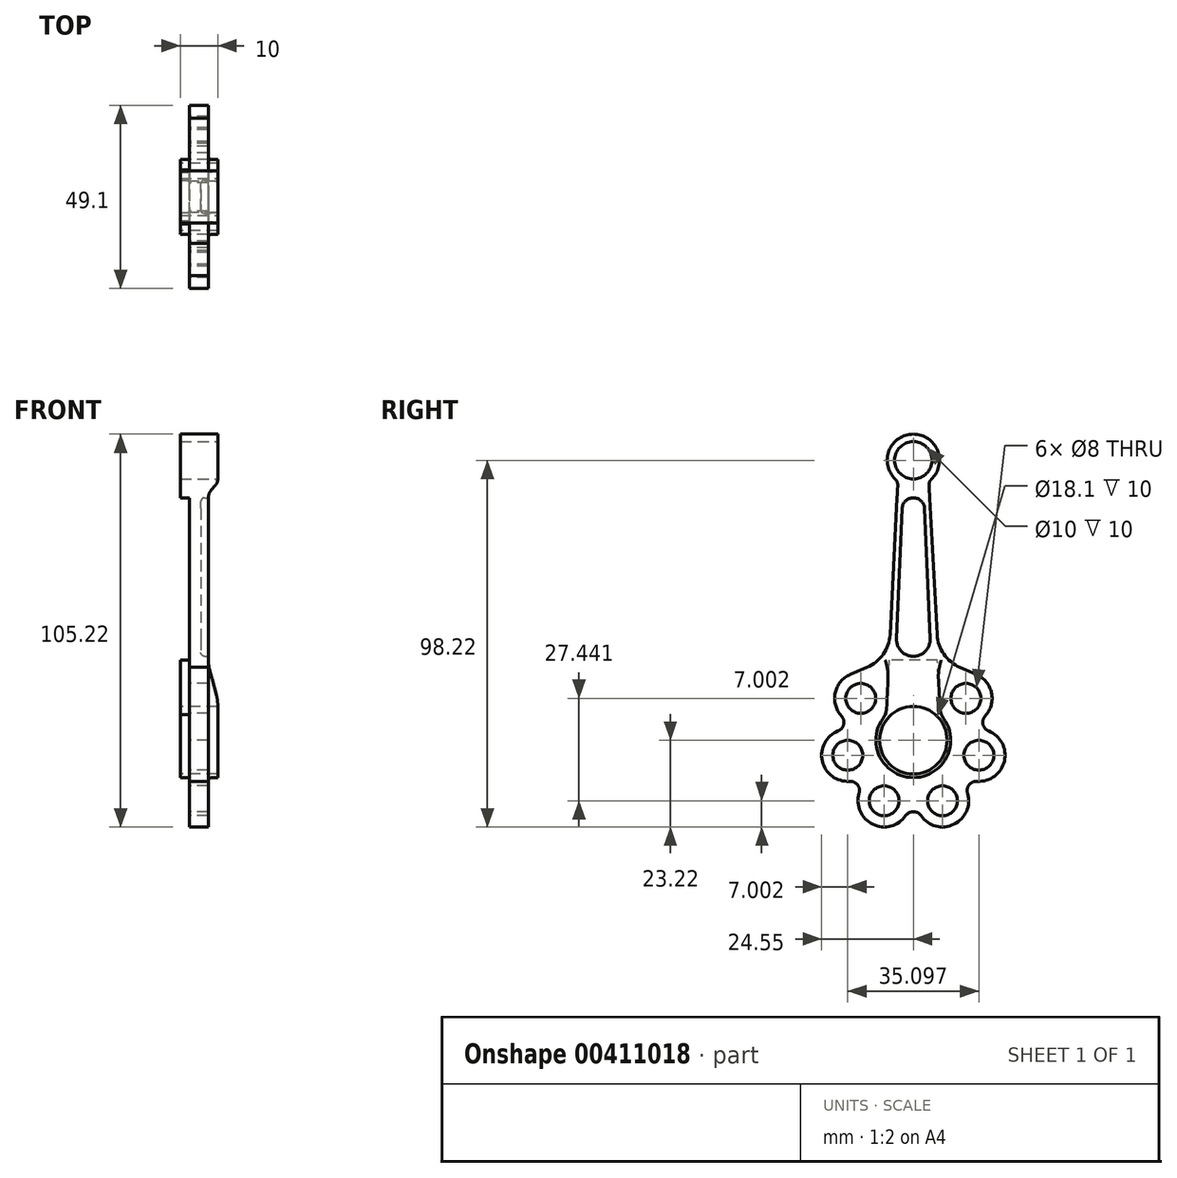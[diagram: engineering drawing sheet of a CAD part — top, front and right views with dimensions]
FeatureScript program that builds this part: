
annotation { "Feature Type Name" : "Feature", "Feature Type Description" : "" }
export const myFeature = defineFeature(function(context is Context, id is Id, definition is map)
    precondition{}
    {
        {
            var Q0;
            Q0=qCreatedBy(makeId("Right.planeOp"),FACE);
            var sketch = newSketch(context, id + "F0", { "sketchPlane" : qUnion([Q0])});
            skArc(sketch, "E0", {"start": v(-16.87, 17.64) * mm, "mid": v(-20.92, 12.68) * mm, "end": v(-19.24, 6.5) * mm});
            skArc(sketch, "E1", {"start": v(-20.15, 2.5) * mm, "mid": v(-24.37, -5.56) * mm, "end": v(-17.08, -11) * mm});
            skArc(sketch, "E2", {"start": v(-14.51, -14.2) * mm, "mid": v(-10.85, -22.53) * mm, "end": v(-2.05, -20.2) * mm});
            skArc(sketch, "E3", {"start": v(2.06, -20.2) * mm, "mid": v(10.85, -22.52) * mm, "end": v(14.52, -14.2) * mm});
            skArc(sketch, "E4", {"start": v(17.08, -11) * mm, "mid": v(24.37, -5.56) * mm, "end": v(20.15, 2.5) * mm});
            skArc(sketch, "E5", {"start": v(-20.15, 2.5) * mm, "mid": v(-18.65, 4.26) * mm, "end": v(-19.24, 6.5) * mm});
            skCircle(sketch, "E6", {"center": v(0, 0) * mm, "radius": 18 * mm, "construction": true});
            skLineSegment(sketch, "E7", {"start": v(0, 0) * mm, "end": v(0, 18) * mm, "construction": true});
            skLineSegment(sketch, "E8", {"start": v(0, 0) * mm, "end": v(-14.07, 11.22) * mm, "construction": true});
            skLineSegment(sketch, "E9", {"start": v(-17.55, -4) * mm, "end": v(0, 0) * mm, "construction": true});
            skLineSegment(sketch, "E10", {"start": v(0, 0) * mm, "end": v(-7.8, -16.22) * mm, "construction": true});
            skLineSegment(sketch, "E11", {"start": v(0, 0) * mm, "end": v(7.81, -16.22) * mm, "construction": true});
            skLineSegment(sketch, "E12", {"start": v(0, 0) * mm, "end": v(17.55, -4) * mm, "construction": true});
            skArc(sketch, "E13", {"start": v(19.24, 6.5) * mm, "mid": v(20.92, 12.68) * mm, "end": v(16.87, 17.64) * mm});
            skLineSegment(sketch, "E14", {"start": v(14.07, 11.22) * mm, "end": v(0, 0) * mm, "construction": true});
            skArc(sketch, "E15", {"start": v(-14.51, -14.2) * mm, "mid": v(-14.95, -11.93) * mm, "end": v(-17.08, -11) * mm});
            skArc(sketch, "E16", {"start": v(2.06, -20.2) * mm, "mid": v(0, -19.13) * mm, "end": v(-2.05, -20.2) * mm});
            skArc(sketch, "E17", {"start": v(17.08, -11) * mm, "mid": v(14.96, -11.93) * mm, "end": v(14.52, -14.2) * mm});
            skArc(sketch, "E18", {"start": v(19.24, 6.5) * mm, "mid": v(18.65, 4.26) * mm, "end": v(20.15, 2.5) * mm});
            skArc(sketch, "E19", {"start": v(4.81, 69.92) * mm, "mid": v(0, 82) * mm, "end": v(-4.81, 69.92) * mm});
            skLineSegment(sketch, "E20", {"start": v(-16.87, 17.64) * mm, "end": v(-12.43, 19.57) * mm});
            skLineSegment(sketch, "E21", {"start": v(12.43, 19.57) * mm, "end": v(16.87, 17.64) * mm});
            skArc(sketch, "E22", {"start": v(-12.43, 19.57) * mm, "mid": v(-8.05, 23.03) * mm, "end": v(-6.2, 28.29) * mm});
            skArc(sketch, "E23", {"start": v(6.37, 28.29) * mm, "mid": v(8.16, 23.07) * mm, "end": v(12.43, 19.57) * mm});
            skLineSegment(sketch, "E24", {"start": v(0, 0) * mm, "end": v(-23.29, 0) * mm, "construction": true});
            skLineSegment(sketch, "E25", {"start": v(-4.19, 68.36) * mm, "end": v(-6.2, 28.29) * mm});
            skLineSegment(sketch, "E26", {"start": v(4.19, 68.35) * mm, "end": v(6.37, 28.29) * mm});
            skArc(sketch, "E27", {"start": v(-4.19, 68.36) * mm, "mid": v(-4.33, 69.2) * mm, "end": v(-4.81, 69.92) * mm});
            skArc(sketch, "E28", {"start": v(4.81, 69.92) * mm, "mid": v(4.33, 69.2) * mm, "end": v(4.19, 68.35) * mm});
            skCircle(sketch, "E29", {"center": v(-14.07, 11.22) * mm, "radius": 4 * mm});
            skCircle(sketch, "E30", {"center": v(-17.55, -4) * mm, "radius": 4 * mm});
            skCircle(sketch, "E31", {"center": v(-7.8, -16.22) * mm, "radius": 4 * mm});
            skCircle(sketch, "E32", {"center": v(7.81, -16.22) * mm, "radius": 4 * mm});
            skCircle(sketch, "E33", {"center": v(17.55, -4) * mm, "radius": 4 * mm});
            skCircle(sketch, "E34", {"center": v(14.07, 11.22) * mm, "radius": 4 * mm});
            skSolve(sketch);
        }
        {
            var Q0;
            Q0 = qSketchRegion(id + "F0", true);
            extrude(context, id + "F1", {"entities" : qUnion([Q0]), "endBound" : BoundingType.SYMMETRIC, "depth" : 5 * mm});
        }
        {
            var Q0;
            Q0=qCreatedBy(makeId("Right.planeOp"),FACE);
            var sketch = newSketch(context, id + "F2", { "sketchPlane" : qUnion([Q0])});
            skArc(sketch, "E35", {"start": v(-7.25, 6.89) * mm, "mid": v(0, -10) * mm, "end": v(7.25, 6.89) * mm});
            skLineSegment(sketch, "E36.bottom", {"start": v(-6.51, 21.5) * mm, "end": v(6.45, 21.5) * mm});
            skLineSegment(sketch, "E37", {"start": v(-7.25, 6.89) * mm, "end": v(-6.51, 21.5) * mm});
            skLineSegment(sketch, "E38", {"start": v(6.45, 21.5) * mm, "end": v(7.25, 6.89) * mm});
            skSolve(sketch);
        }
        {
            var Q0;
            Q0 = qSketchRegion(id + "F2", true);
            extrude(context, id + "F3", {"entities" : qUnion([Q0]), "operationType" : NewBodyOperationType.ADD, "endBound" : BoundingType.SYMMETRIC, "depth" : 10 * mm});
        }
        {
            var Q0;
            Q0=makeQuery(id+"F1.opExtrude","CAP_FACE",FACE,{"disambiguationData":[OSD([sQuery(id+"F0.wireOp",EDGE,"E0"),sQuery(id+"F0.wireOp",EDGE,"E1"),sQuery(id+"F0.wireOp",EDGE,"E2"),sQuery(id+"F0.wireOp",EDGE,"E3"),sQuery(id+"F0.wireOp",EDGE,"E4"),sQuery(id+"F0.wireOp",EDGE,"E5"),sQuery(id+"F0.wireOp",EDGE,"E13"),sQuery(id+"F0.wireOp",EDGE,"E15"),sQuery(id+"F0.wireOp",EDGE,"E16"),sQuery(id+"F0.wireOp",EDGE,"E17"),sQuery(id+"F0.wireOp",EDGE,"E18"),sQuery(id+"F0.wireOp",EDGE,"E19"),sQuery(id+"F0.wireOp",EDGE,"E20"),sQuery(id+"F0.wireOp",EDGE,"E21"),sQuery(id+"F0.wireOp",EDGE,"E22"),sQuery(id+"F0.wireOp",EDGE,"E23"),sQuery(id+"F0.wireOp",EDGE,"E25"),sQuery(id+"F0.wireOp",EDGE,"E26"),sQuery(id+"F0.wireOp",EDGE,"E27"),sQuery(id+"F0.wireOp",EDGE,"E28")])],"isStart":false});
            var sketch = newSketch(context, id + "F4", { "sketchPlane" : qUnion([Q0])});
            skArc(sketch, "E39", {"start": v(-4.5, 27.2) * mm, "mid": v(0, 22.5) * mm, "end": v(4.5, 27.2) * mm});
            skArc(sketch, "E40", {"start": v(3, 62.1) * mm, "mid": v(0, 64.97) * mm, "end": v(-3, 62.1) * mm});
            skLineSegment(sketch, "E41", {"start": v(-3, 62.1) * mm, "end": v(-4.5, 27.2) * mm});
            skLineSegment(sketch, "E42", {"start": v(3, 62.1) * mm, "end": v(4.5, 27.2) * mm});
            skCircle(sketch, "E43", {"center": v(0, 75) * mm, "radius": 2 * mm, "construction": true});
            skSolve(sketch);
        }
        {
            var Q0;
            Q0 = qSketchRegion(id + "F4", true);
            extrude(context, id + "F5", {"entities" : qUnion([Q0]), "operationType" : NewBodyOperationType.REMOVE, "oppositeDirection" : true, "depth" : 2 * mm});
        }
        {
            var Q0;
            Q0=makeQuery(id+"F5.boolean.opBoolean","COPY",FACE,{"derivedFrom":makeQuery(id+"F5.opExtrude","CAP_FACE",FACE,{"disambiguationData":[OSD([sQuery(id+"F4.wireOp",EDGE,"E39"),sQuery(id+"F4.wireOp",EDGE,"E40"),sQuery(id+"F4.wireOp",EDGE,"E41"),sQuery(id+"F4.wireOp",EDGE,"E42")])],"isStart":false})});
            fillet(context, id + "F6", {"entities" : qUnion([Q0]), "radius" : 1 * mm, "tangentPropagation" : true, "allowEdgeOverflow" : false});
        }
        {
            var Q0;
            Q0=qCreatedBy(makeId("Right.planeOp"),FACE);
            var sketch = newSketch(context, id + "F7", { "sketchPlane" : qUnion([Q0])});
            skCircle(sketch, "E44", {"center": v(0, 0) * mm, "radius": 9.05 * mm});
            skSolve(sketch);
        }
        {
            var Q0;
            Q0 = qSketchRegion(id + "F7", true);
            extrude(context, id + "F8", {"entities" : qUnion([Q0]), "operationType" : NewBodyOperationType.REMOVE, "endBound" : BoundingType.SYMMETRIC, "depth" : 25 * mm});
        }
        {
            var Q0;
            Q0=qCreatedBy(makeId("Front.planeOp"),FACE);
            var sketch = newSketch(context, id + "F9", { "sketchPlane" : qUnion([Q0])});
            skLineSegment(sketch, "E45", {"start": v(4.66, 12.13) * mm, "end": v(2.84, 18.91) * mm});
            skLineSegment(sketch, "E46", {"start": v(2.5, 21.5) * mm, "end": v(2.5, 24) * mm, "construction": true});
            skArc(sketch, "E47", {"start": v(21.38, -48.57) * mm, "mid": v(20.84, -45.33) * mm, "end": v(19.28, -42.44) * mm});
            skArc(sketch, "E48", {"start": v(2.5, 21.5) * mm, "mid": v(2.59, 20.2) * mm, "end": v(2.84, 18.91) * mm});
            skLineSegment(sketch, "E49", {"start": v(5, 9.54) * mm, "end": v(5, 21.5) * mm});
            skLineSegment(sketch, "E50.trimOffspring", {"start": v(5, 21.5) * mm, "end": v(2.5, 21.5) * mm});
            skArc(sketch, "E51", {"start": v(5, 9.54) * mm, "mid": v(4.91, 10.84) * mm, "end": v(4.66, 12.13) * mm});
            skSolve(sketch);
        }
        {
            var Q0;
            Q0 = qSketchRegion(id + "F9", true);
            extrude(context, id + "F10", {"entities" : qUnion([Q0]), "operationType" : NewBodyOperationType.REMOVE, "endBound" : BoundingType.SYMMETRIC, "oppositeDirection" : true, "depth" : 25 * mm, "hasSecondDirection" : true, "secondDirectionOppositeDirection" : false, "secondDirectionDepth" : 25 * mm});
        }
        {
            var Q0;
            {var subQ0=sQuery(id+"F2.wireOp",EDGE,"E35");var subQ1=sQuery(id+"F2.wireOp",EDGE,"E36.right");Q0=makeQuery(id+"F3.boolean.opBoolean","SPLIT",EDGE,{"disambiguationData":[TD([makeQuery(id+"F3.opExtrude","CAP_FACE",FACE,{"disambiguationData":[OSD([subQ0,sQuery(id+"F2.wireOp",EDGE,"E36.bottom"),sQuery(id+"F2.wireOp",EDGE,"E36.left"),subQ1])],"isStart":false})])],"derivedFrom":makeQuery(id+"F3.opExtrude","SWEPT_EDGE",EDGE,{"disambiguationData":[OSD([subQ0,subQ1])]})});}
            var Q1;
            {var subQ0=sQuery(id+"F2.wireOp",EDGE,"E36.left");var subQ1=sQuery(id+"F2.wireOp",EDGE,"E35");Q1=makeQuery(id+"F3.boolean.opBoolean","SPLIT",EDGE,{"disambiguationData":[TD([makeQuery(id+"F3.opExtrude","CAP_FACE",FACE,{"disambiguationData":[OSD([subQ1,sQuery(id+"F2.wireOp",EDGE,"E36.bottom"),subQ0,sQuery(id+"F2.wireOp",EDGE,"E36.right")])],"isStart":false})])],"derivedFrom":makeQuery(id+"F3.opExtrude","SWEPT_EDGE",EDGE,{"disambiguationData":[OSD([subQ1,subQ0])]})});}
            fillet(context, id + "F11", {"entities" : qUnion([Q0, Q1]), "radius" : 5 * mm, "tangentPropagation" : true, "allowEdgeOverflow" : false});
        }
        {
            var Q0;
            Q0=makeQuery(id+"F3.boolean.opBoolean","INTERSECT",EDGE,{"derivedFrom":[makeQuery(id+"F1.opExtrude","CAP_FACE",FACE,{"disambiguationData":[OSD([sQuery(id+"F0.wireOp",EDGE,"E0"),sQuery(id+"F0.wireOp",EDGE,"E1"),sQuery(id+"F0.wireOp",EDGE,"E2"),sQuery(id+"F0.wireOp",EDGE,"E3"),sQuery(id+"F0.wireOp",EDGE,"E4"),sQuery(id+"F0.wireOp",EDGE,"E5"),sQuery(id+"F0.wireOp",EDGE,"E13"),sQuery(id+"F0.wireOp",EDGE,"E15"),sQuery(id+"F0.wireOp",EDGE,"E16"),sQuery(id+"F0.wireOp",EDGE,"E17"),sQuery(id+"F0.wireOp",EDGE,"E18"),sQuery(id+"F0.wireOp",EDGE,"E19"),sQuery(id+"F0.wireOp",EDGE,"E20"),sQuery(id+"F0.wireOp",EDGE,"E21"),sQuery(id+"F0.wireOp",EDGE,"E22"),sQuery(id+"F0.wireOp",EDGE,"E23"),sQuery(id+"F0.wireOp",EDGE,"E25"),sQuery(id+"F0.wireOp",EDGE,"E26"),sQuery(id+"F0.wireOp",EDGE,"E27"),sQuery(id+"F0.wireOp",EDGE,"E28")])],"isStart":false}),makeQuery(id+"F3.opExtrude","SWEPT_FACE",FACE,{"disambiguationData":[OSD([sQuery(id+"F2.wireOp",EDGE,"E36.left")])]})]});
            var Q1;
            {var subQ0=makeQuery(id+"F1.opExtrude","CAP_FACE",FACE,{"disambiguationData":[OSD([sQuery(id+"F0.wireOp",EDGE,"E0"),sQuery(id+"F0.wireOp",EDGE,"E1"),sQuery(id+"F0.wireOp",EDGE,"E2"),sQuery(id+"F0.wireOp",EDGE,"E3"),sQuery(id+"F0.wireOp",EDGE,"E4"),sQuery(id+"F0.wireOp",EDGE,"E5"),sQuery(id+"F0.wireOp",EDGE,"E13"),sQuery(id+"F0.wireOp",EDGE,"E15"),sQuery(id+"F0.wireOp",EDGE,"E16"),sQuery(id+"F0.wireOp",EDGE,"E17"),sQuery(id+"F0.wireOp",EDGE,"E18"),sQuery(id+"F0.wireOp",EDGE,"E19"),sQuery(id+"F0.wireOp",EDGE,"E20"),sQuery(id+"F0.wireOp",EDGE,"E21"),sQuery(id+"F0.wireOp",EDGE,"E22"),sQuery(id+"F0.wireOp",EDGE,"E23"),sQuery(id+"F0.wireOp",EDGE,"E25"),sQuery(id+"F0.wireOp",EDGE,"E26"),sQuery(id+"F0.wireOp",EDGE,"E27"),sQuery(id+"F0.wireOp",EDGE,"E28")])],"isStart":false});var subQ1=sQuery(id+"F2.wireOp",EDGE,"E36.left");var subQ2=sQuery(id+"F2.wireOp",EDGE,"E35");Q1=makeQuery(id+"F11.opFillet","BLEND_EDGE",EDGE,{"blendedFrom":[makeQuery(id+"F3.boolean.opBoolean","SPLIT",EDGE,{"disambiguationData":[TD([makeQuery(id+"F3.opExtrude","CAP_FACE",FACE,{"disambiguationData":[OSD([subQ2,sQuery(id+"F2.wireOp",EDGE,"E36.bottom"),subQ1,sQuery(id+"F2.wireOp",EDGE,"E36.right")])],"isStart":false})])],"derivedFrom":makeQuery(id+"F3.opExtrude","SWEPT_EDGE",EDGE,{"disambiguationData":[OSD([subQ2,subQ1])]})}),subQ0],"blendedInto":[subQ0]});}
            fillet(context, id + "F12", {"entities" : qUnion([Q0, Q1]), "radius" : 1 * mm, "tangentPropagation" : true, "allowEdgeOverflow" : false});
        }
        {
            var Q0;
            Q0=qCreatedBy(makeId("Right.planeOp"),FACE);
            var sketch = newSketch(context, id + "F13", { "sketchPlane" : qUnion([Q0])});
            skLineSegment(sketch, "E52.top", {"start": v(4.37, 64.97) * mm, "end": v(-4.36, 64.97) * mm});
            skArc(sketch, "E53", {"start": v(4.81, 69.92) * mm, "mid": v(0, 82) * mm, "end": v(-4.81, 69.92) * mm});
            skArc(sketch, "E54", {"start": v(-4.19, 68.36) * mm, "mid": v(-4.33, 69.2) * mm, "end": v(-4.81, 69.92) * mm});
            skArc(sketch, "E55", {"start": v(4.81, 69.92) * mm, "mid": v(4.33, 69.2) * mm, "end": v(4.19, 68.35) * mm});
            skLineSegment(sketch, "E56", {"start": v(-4.19, 68.36) * mm, "end": v(-4.36, 64.97) * mm});
            skLineSegment(sketch, "E57", {"start": v(4.37, 64.97) * mm, "end": v(4.19, 68.35) * mm});
            skSolve(sketch);
        }
        {
            var Q0;
            Q0 = qSketchRegion(id + "F13", true);
            extrude(context, id + "F14", {"entities" : qUnion([Q0]), "operationType" : NewBodyOperationType.ADD, "endBound" : BoundingType.SYMMETRIC, "depth" : 10 * mm});
        }
        {
            var Q0;
            Q0=qCreatedBy(makeId("Front.planeOp"),FACE);
            var sketch = newSketch(context, id + "F15", { "sketchPlane" : qUnion([Q0])});
            skLineSegment(sketch, "E58", {"start": v(2.5, 64.97) * mm, "end": v(5, 64.97) * mm});
            skLineSegment(sketch, "E59", {"start": v(5, 64.97) * mm, "end": v(5, 69.77) * mm});
            skLineSegment(sketch, "E60", {"start": v(3.2, 66.9) * mm, "end": v(4.53, 68.48) * mm});
            skArc(sketch, "E61", {"start": v(4.53, 68.48) * mm, "mid": v(4.88, 69.09) * mm, "end": v(5, 69.77) * mm});
            skLineSegment(sketch, "E62", {"start": v(2.5, 64.97) * mm, "end": v(2.5, 62.47) * mm, "construction": true});
            skArc(sketch, "E63", {"start": v(3.2, 66.9) * mm, "mid": v(2.68, 66) * mm, "end": v(2.5, 64.97) * mm});
            skSolve(sketch);
        }
        {
            var Q0;
            Q0 = qSketchRegion(id + "F15", true);
            extrude(context, id + "F16", {"entities" : qUnion([Q0]), "operationType" : NewBodyOperationType.REMOVE, "endBound" : BoundingType.SYMMETRIC, "depth" : 25 * mm});
        }
        {
            var Q0;
            Q0=makeQuery(id+"F14.opExtrude","CAP_FACE",FACE,{"disambiguationData":[OSD([sQuery(id+"F13.wireOp",EDGE,"E52.top"),sQuery(id+"F13.wireOp",EDGE,"E53"),sQuery(id+"F13.wireOp",EDGE,"E54"),sQuery(id+"F13.wireOp",EDGE,"E55"),sQuery(id+"F13.wireOp",EDGE,"E56"),sQuery(id+"F13.wireOp",EDGE,"E57")])],"isStart":false});
            var sketch = newSketch(context, id + "F17", { "sketchPlane" : qUnion([Q0])});
            skCircle(sketch, "E64", {"center": v(0, 75) * mm, "radius": 5 * mm});
            skSolve(sketch);
        }
        {
            var Q0;
            Q0 = qSketchRegion(id + "F17", true);
            extrude(context, id + "F18", {"entities" : qUnion([Q0]), "operationType" : NewBodyOperationType.REMOVE, "oppositeDirection" : true, "depth" : 25 * mm});
        }
    });
